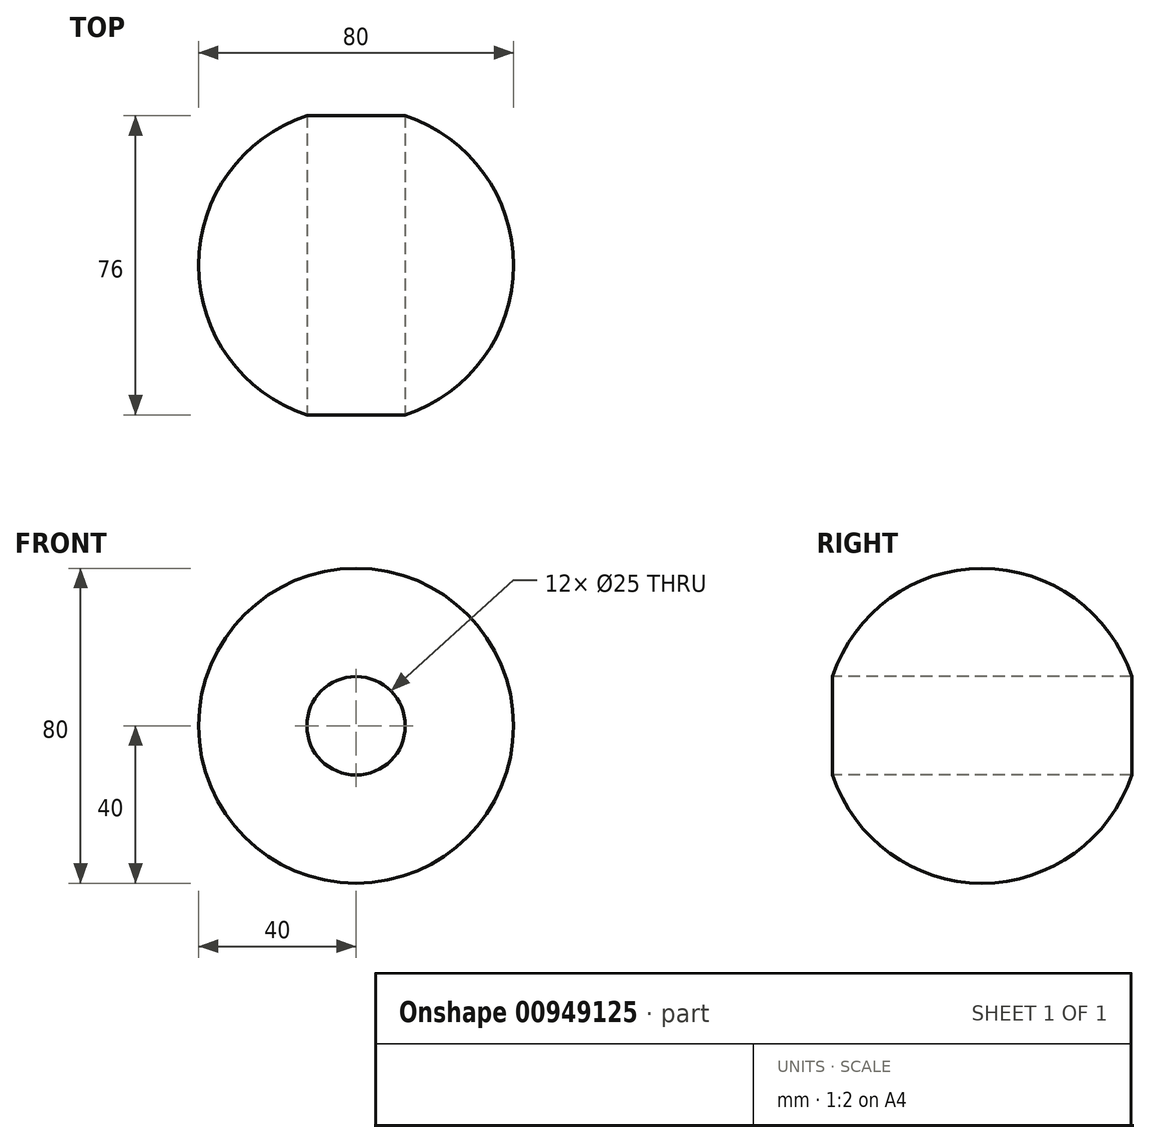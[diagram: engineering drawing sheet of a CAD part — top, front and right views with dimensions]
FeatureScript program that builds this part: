
annotation { "Feature Type Name" : "Feature", "Feature Type Description" : "" }
export const myFeature = defineFeature(function(context is Context, id is Id, definition is map)
    precondition{}
    {
        {
            var Q0;
            Q0=qCreatedBy(makeId("Top.planeOp"),FACE);
            var sketch = newSketch(context, id + "F0", { "sketchPlane" : qUnion([Q0])});
            skArc(sketch, "E0", {"start": v(0, -40) * mm, "mid": v(40, 0) * mm, "end": v(0, 40) * mm});
            skLineSegment(sketch, "E1", {"start": v(0, 40) * mm, "end": v(0, -40) * mm});
            skSolve(sketch);
        }
        {
            var Q0;
            Q0=makeQuery(id+"F0.imprint","IMPRINT",FACE,{"disambiguationData":[TD([[makeQuery(id+"F0.imprint","IMPRINT",EDGE,{"derivedFrom":sQuery(id+"F0.wireOp",EDGE,"E0")}),1.0]])]});
            var Q1;
            Q1=sQuery(id+"F0.wireOp",EDGE,"E1");
            revolve(context, id + "F1", {"surfaceOperationType" : NewSurfaceOperationType.NEW, "entities" : qUnion([Q0]), "axis" : qUnion([Q1]), "revolveType" : RevolveType.FULL});
        }
        {
            var Q0;
            Q0=qCreatedBy(makeId("Front.planeOp"),FACE);
            var sketch = newSketch(context, id + "F2", { "sketchPlane" : qUnion([Q0])});
            skCircle(sketch, "E2", {"center": v(0, 0) * mm, "radius": 12.5 * mm});
            skSolve(sketch);
        }
        {
            var Q0;
            Q0 = qSketchRegion(id + "F2", true);
            extrude(context, id + "F3", {"entities" : qUnion([Q0]), "operationType" : NewBodyOperationType.REMOVE, "endBound" : BoundingType.SYMMETRIC, "oppositeDirection" : true, "depth" : 100 * mm, "offsetDistance" : 25.4 * mm});
        }
    });
